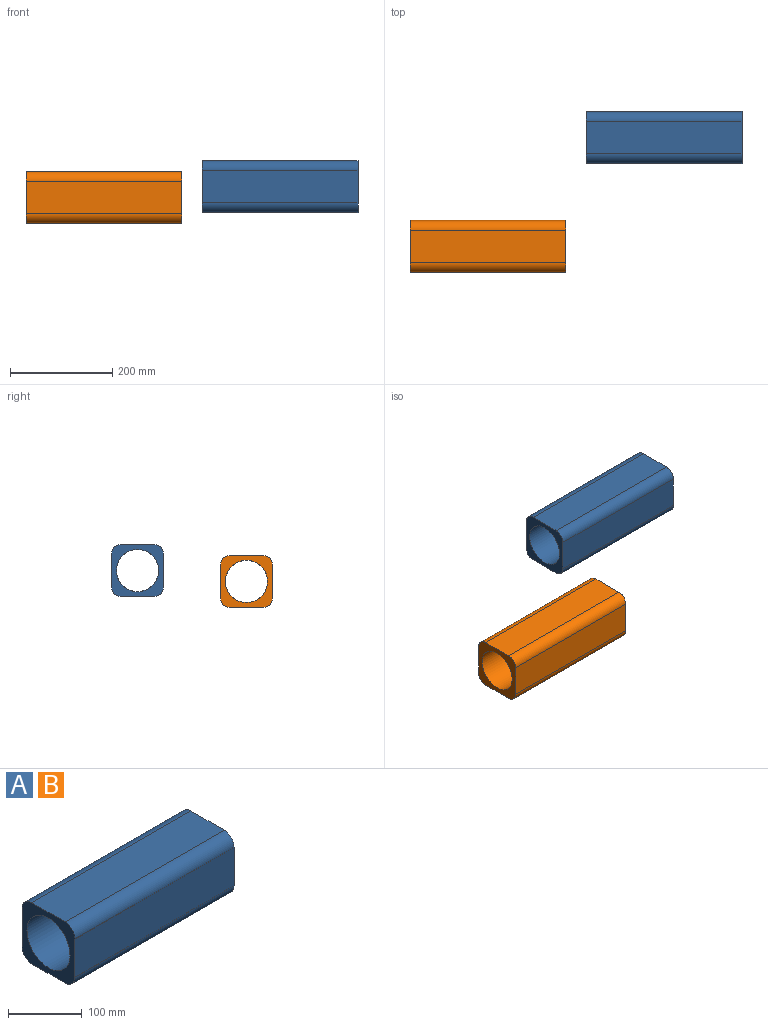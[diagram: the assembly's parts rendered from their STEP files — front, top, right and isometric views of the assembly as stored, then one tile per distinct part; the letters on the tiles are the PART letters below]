
ASSEMBLY  parts=2 mates=1
PART A: 11 faces, bbox 304.8x101.6x101.6 mm
  f0: plane 304.8x63.5mm, normal (0,-1,0), area 19354.8mm2, adj f1,f3,f8,f10
  f1: plane 101.6x101.6mm, normal (1,0,0), area 4658.9mm2, adj f0,f2,f4,f5,f6,f7,f8,f9
  f2: plane 304.8x63.5mm, normal (0,1,0), area 19354.8mm2, adj f1,f3,f7,f9
  f3: plane 101.6x101.6mm, normal (-1,0,0), area 4658.9mm2, adj f0,f2,f4,f5,f6,f7,f8,f9
  f4: plane 304.8x63.5mm, normal (0,0,1), area 19354.8mm2, adj f1,f3,f9,f10
  f5: plane 304.8x63.5mm, normal (0,0,-1), area 19354.8mm2, adj f1,f3,f7,f8
  f6: cylinder r=41.27mm len=304.8mm, axis (1,0,0), area 79046.4mm2, adj f1,f3
  f7: cylinder r=19.05mm len=304.8mm, axis (-1,0,0), area 9120.7mm2, adj f1,f2,f3,f5
  f8: cylinder r=19.05mm len=304.8mm, axis (1,0,0), area 9120.7mm2, adj f0,f1,f3,f5
  f9: cylinder r=19.05mm len=304.8mm, axis (1,0,0), area 9120.7mm2, adj f1,f2,f3,f4
  f10: cylinder r=19.05mm len=304.8mm, axis (-1,0,0), area 9120.7mm2, adj f0,f1,f3,f4
PART B: same geometry as A
PLACE A t=(10.07,20.89,22.61)mm
PLACE B t=(-334.06,-192.09,1.17)mm
MATE parallel A.f9 <-> B.f9  axis (1,0,0) through (162.47,52.64,54.36)mm
